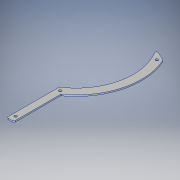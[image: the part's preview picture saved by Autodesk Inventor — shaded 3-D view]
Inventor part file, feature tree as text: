
AUTODESK INVENTOR PART (.ipt)
format: ipt  version: 2017 (Build 210142000, 142)  size: 141,312 bytes
history: native  units: in
note: dims shown in document units (in); Inventor stores cm internally (conversion verified against a paired STEP export)
features: sketch x2, extrude x1, hole x1
ambient origin geometry x8: Origin, YZ Plane, XZ Plane, XY Plane, X Axis, Y Axis, Z Axis, Center Point
bodies: Solid1 (feature_tree)
feature tree (4):
  extrude  "Extrusion1"  Depth=5.2in
  hole  "Hole1"  [1 undecoded]
  sketch  "Sketch1"  dims[d1=5.2in d2=0.2272in]
  sketch  "Sketch2"  dims[d3=0.5978in d4=11.9in d5=1.152in d6=4.75in d8=0.125in d9=0.125in d10=0.125in d11=0.125in d12=0.0in d13=11.15in d14=0.25in d15=0.25in d16=0.25in d17=0.5in d19=0.25in d20=0.75in d21=0.375in d22=0.25in d23=0.5635in d24=1.0in d25=0.8108in]
note: 1 required parameter value undecoded (feature->parameter linkage not recoverable at this tier; creation-order binding heuristic only, values carry confidence <= 0.55)
